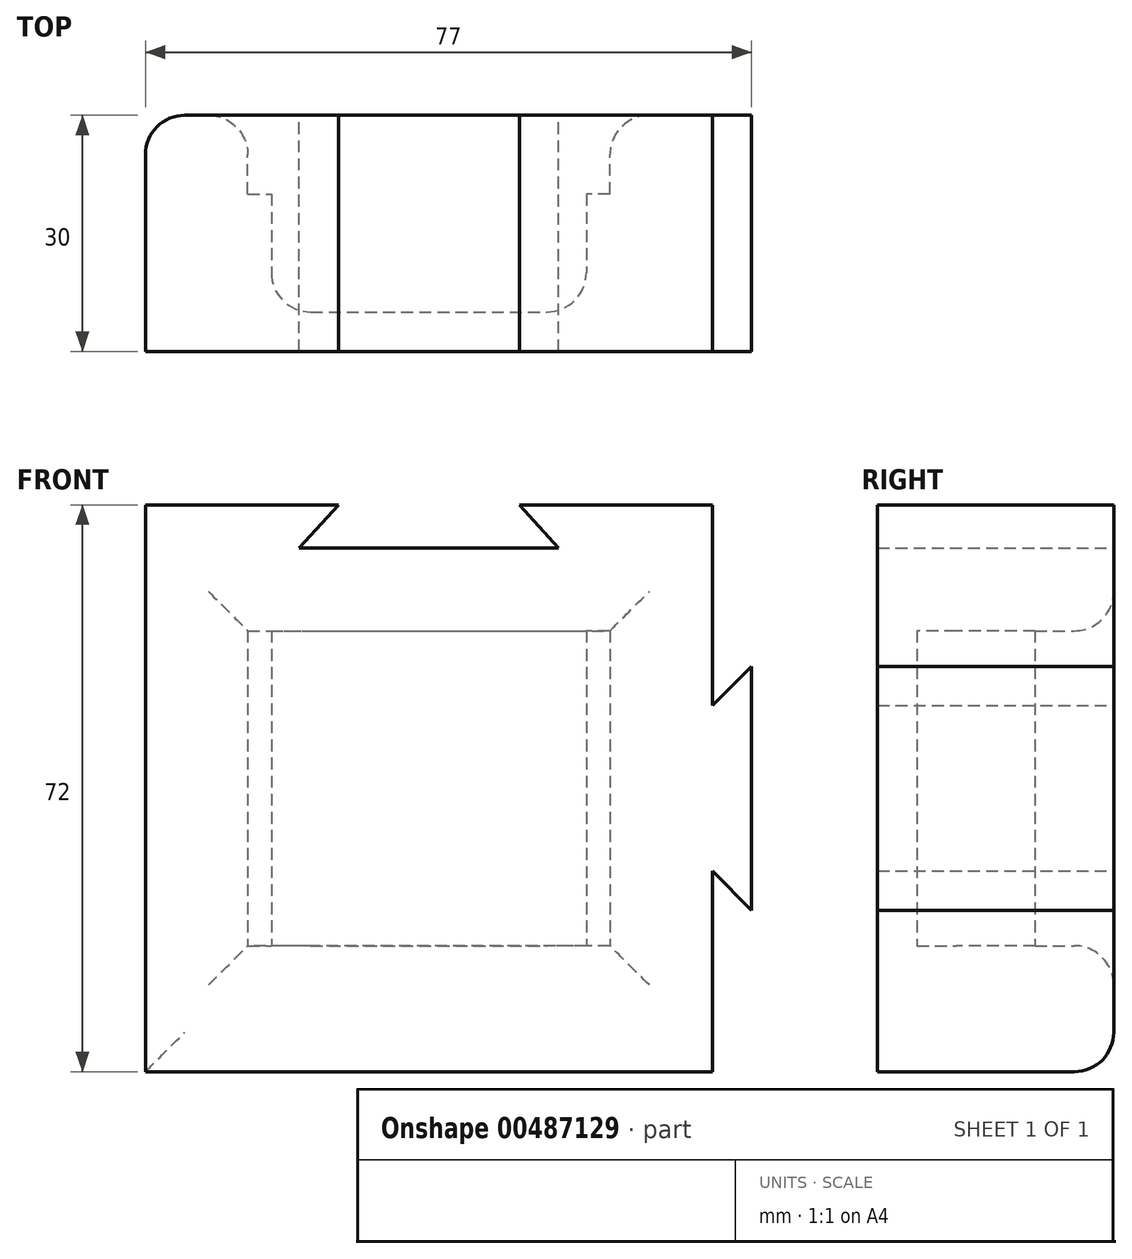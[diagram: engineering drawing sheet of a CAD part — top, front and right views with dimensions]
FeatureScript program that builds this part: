
annotation { "Feature Type Name" : "Feature", "Feature Type Description" : "" }
export const myFeature = defineFeature(function(context is Context, id is Id, definition is map)
    precondition{}
    {
        {
            var Q0;
            Q0=qCreatedBy(makeId("Top.planeOp"),FACE);
            var sketch = newSketch(context, id + "F0", { "sketchPlane" : qUnion([Q0])});
            skLineSegment(sketch, "E0.top", {"start": v(-25, -20) * mm, "end": v(25, -20) * mm});
            skLineSegment(sketch, "E0.left", {"start": v(-25, 0) * mm, "end": v(-25, -20) * mm});
            skLineSegment(sketch, "E0.right", {"start": v(25, 0) * mm, "end": v(25, -20) * mm});
            skLineSegment(sketch, "E1.bottom", {"start": v(-25, 0) * mm, "end": v(-23, 0) * mm});
            skLineSegment(sketch, "E1.top", {"start": v(-25, 10) * mm, "end": v(-23, 10) * mm});
            skLineSegment(sketch, "E1.left", {"start": v(-25, 0) * mm, "end": v(-25, 10) * mm});
            skLineSegment(sketch, "E1.right", {"start": v(-23, 0) * mm, "end": v(-23, 10) * mm});
            skLineSegment(sketch, "E2.bottom", {"start": v(25, 0) * mm, "end": v(23, 0) * mm});
            skLineSegment(sketch, "E2.top", {"start": v(25, 10) * mm, "end": v(23, 10) * mm});
            skLineSegment(sketch, "E2.left", {"start": v(25, 0) * mm, "end": v(25, 10) * mm});
            skLineSegment(sketch, "E2.right", {"start": v(23, 0) * mm, "end": v(23, 10) * mm});
            skLineSegment(sketch, "E3", {"start": v(-25, 0) * mm, "end": v(-20, 0) * mm});
            skLineSegment(sketch, "E4", {"start": v(25, 0) * mm, "end": v(20, 0) * mm});
            skLineSegment(sketch, "E5.bottom", {"start": v(-20, 0) * mm, "end": v(20, 0) * mm});
            skLineSegment(sketch, "E5.top", {"start": v(-20, -15) * mm, "end": v(20, -15) * mm});
            skLineSegment(sketch, "E5.left", {"start": v(-20, 0) * mm, "end": v(-20, -15) * mm});
            skLineSegment(sketch, "E5.right", {"start": v(20, 0) * mm, "end": v(20, -15) * mm});
            skSolve(sketch);
        }
        {
            var Q0;
            Q0=makeQuery(id+"F0.imprint","IMPRINT",FACE,{"disambiguationData":[TD([[makeQuery(id+"F0.imprint","IMPRINT",EDGE,{"derivedFrom":sQuery(id+"F0.wireOp",EDGE,"E1.top")}),-1.0]])]});
            var Q1;
            Q1=makeQuery(id+"F0.imprint","IMPRINT",FACE,{"disambiguationData":[TD([[makeQuery(id+"F0.imprint","IMPRINT",EDGE,{"derivedFrom":sQuery(id+"F0.wireOp",EDGE,"E2.top")}),1.0]])]});
            var Q2;
            Q2=makeQuery(id+"F0.imprint","IMPRINT",FACE,{"disambiguationData":[TD([[makeQuery(id+"F0.imprint","IMPRINT",EDGE,{"derivedFrom":sQuery(id+"F0.wireOp",EDGE,"E0.top")}),1.0]])]});
            extrude(context, id + "F1", {"entities" : qUnion([Q0, Q1, Q2]), "depth" : 40 * mm});
        }
        {
            var Q0;
            Q0=makeQuery(id+"F1.opExtrude","CAP_FACE",FACE,{"disambiguationData":[OSD([sQuery(id+"F0.wireOp",EDGE,"E0.top"),sQuery(id+"F0.wireOp",EDGE,"E0.left"),sQuery(id+"F0.wireOp",EDGE,"E0.right"),sQuery(id+"F0.wireOp",EDGE,"99edbcf1-32be-412c-bc92-f7043755eeb8.trimOffspring"),sQuery(id+"F0.wireOp",EDGE,"E1.top"),sQuery(id+"F0.wireOp",EDGE,"E1.left"),sQuery(id+"F0.wireOp",EDGE,"E1.right"),sQuery(id+"F0.wireOp",EDGE,"E2.top"),sQuery(id+"F0.wireOp",EDGE,"E2.left"),sQuery(id+"F0.wireOp",EDGE,"E2.right"),sQuery(id+"F0.wireOp",EDGE,"E3"),sQuery(id+"F0.wireOp",EDGE,"AQl3pC6e-wCTG-qIrR-r3pU-YnEMlh3t2a7q")])],"isStart":false});
            var sketch = newSketch(context, id + "F2", { "sketchPlane" : qUnion([Q0])});
            skLineSegment(sketch, "E6.bottom", {"start": v(-25, 10) * mm, "end": v(25, 10) * mm});
            skLineSegment(sketch, "E6.top", {"start": v(-25, -20) * mm, "end": v(25, -20) * mm});
            skLineSegment(sketch, "E6.left", {"start": v(-25, 10) * mm, "end": v(-25, -20) * mm});
            skLineSegment(sketch, "E6.right", {"start": v(25, 10) * mm, "end": v(25, -20) * mm});
            skSolve(sketch);
        }
        {
            var Q0;
            Q0 = qSketchRegion(id + "F2", true);
            extrude(context, id + "F3", {"entities" : qUnion([Q0]), "operationType" : NewBodyOperationType.ADD, "depth" : 5 * mm});
        }
        {
            var Q0;
            Q0=makeQuery(id+"F1.opExtrude","CAP_FACE",FACE,{"disambiguationData":[OSD([sQuery(id+"F0.wireOp",EDGE,"E0.top"),sQuery(id+"F0.wireOp",EDGE,"E0.left"),sQuery(id+"F0.wireOp",EDGE,"E0.right"),sQuery(id+"F0.wireOp",EDGE,"99edbcf1-32be-412c-bc92-f7043755eeb8.trimOffspring"),sQuery(id+"F0.wireOp",EDGE,"E1.top"),sQuery(id+"F0.wireOp",EDGE,"E1.left"),sQuery(id+"F0.wireOp",EDGE,"E1.right"),sQuery(id+"F0.wireOp",EDGE,"E2.top"),sQuery(id+"F0.wireOp",EDGE,"E2.left"),sQuery(id+"F0.wireOp",EDGE,"E2.right"),sQuery(id+"F0.wireOp",EDGE,"E3"),sQuery(id+"F0.wireOp",EDGE,"AQl3pC6e-wCTG-qIrR-r3pU-YnEMlh3t2a7q")])],"isStart":true});
            var sketch = newSketch(context, id + "F4", { "sketchPlane" : qUnion([Q0])});
            skLineSegment(sketch, "E7.bottom", {"start": v(25, -10) * mm, "end": v(-25, -10) * mm});
            skLineSegment(sketch, "E7.top", {"start": v(25, 20) * mm, "end": v(-25, 20) * mm});
            skLineSegment(sketch, "E7.left", {"start": v(25, -10) * mm, "end": v(25, 20) * mm});
            skLineSegment(sketch, "E7.right", {"start": v(-25, -10) * mm, "end": v(-25, 20) * mm});
            skSolve(sketch);
        }
        {
            var Q0;
            Q0 = qSketchRegion(id + "F4", true);
            extrude(context, id + "F5", {"entities" : qUnion([Q0]), "operationType" : NewBodyOperationType.ADD, "depth" : 5 * mm});
        }
        {
            var Q0;
            Q0=makeQuery(id+"F5.boolean.opBoolean","MERGE",FACE,{"derivedFrom":[makeQuery(id+"F3.boolean.opBoolean","MERGE",FACE,{"derivedFrom":[makeQuery(id+"F1.opExtrude","SWEPT_FACE",FACE,{"disambiguationData":[OSD([sQuery(id+"F0.wireOp",EDGE,"E1.top")])]}),makeQuery(id+"F1.opExtrude","SWEPT_FACE",FACE,{"disambiguationData":[OSD([sQuery(id+"F0.wireOp",EDGE,"E2.top")])]}),makeQuery(id+"F3.opExtrude","SWEPT_FACE",FACE,{"disambiguationData":[OSD([sQuery(id+"F2.wireOp",EDGE,"E6.bottom")])]})]}),makeQuery(id+"F5.opExtrude","SWEPT_FACE",FACE,{"disambiguationData":[OSD([sQuery(id+"F4.wireOp",EDGE,"E7.bottom")])]})]});
            var sketch = newSketch(context, id + "F6", { "sketchPlane" : qUnion([Q0])});
            skLineSegment(sketch, "E8.bottom", {"start": v(-25, -5) * mm, "end": v(25, -5) * mm});
            skLineSegment(sketch, "E8.top", {"start": v(-25, 45) * mm, "end": v(25, 45) * mm});
            skLineSegment(sketch, "E8.left", {"start": v(-25, -5) * mm, "end": v(-25, 45) * mm});
            skLineSegment(sketch, "E8.right", {"start": v(25, -5) * mm, "end": v(25, 45) * mm});
            skLineSegment(sketch, "E9.bottom", {"start": v(-36, -16) * mm, "end": v(36, -16) * mm});
            skLineSegment(sketch, "E9.top", {"start": v(-36, 56) * mm, "end": v(36, 56) * mm});
            skLineSegment(sketch, "E9.left", {"start": v(-36, -16) * mm, "end": v(-36, 56) * mm});
            skLineSegment(sketch, "E9.right", {"start": v(36, -16) * mm, "end": v(36, 56) * mm});
            skLineSegment(sketch, "E10", {"start": v(-36, 30.5) * mm, "end": v(-41, 35.5) * mm});
            skLineSegment(sketch, "E11", {"start": v(-41, 35.5) * mm, "end": v(-41, 4.5) * mm});
            skLineSegment(sketch, "E12", {"start": v(-41, 4.5) * mm, "end": v(-36, 9.5) * mm});
            skLineSegment(sketch, "E13", {"start": v(-11.5, 56) * mm, "end": v(-16.5, 50.5) * mm});
            skLineSegment(sketch, "E14", {"start": v(-16.5, 50.5) * mm, "end": v(16.5, 50.5) * mm});
            skLineSegment(sketch, "E15", {"start": v(16.5, 50.5) * mm, "end": v(11.5, 56) * mm});
            skSolve(sketch);
        }
        {
            var Q0;
            Q0=makeQuery(id+"F6.imprint","IMPRINT",FACE,{"disambiguationData":[TD([[makeQuery(id+"F6.imprint","IMPRINT",EDGE,{"derivedFrom":sQuery(id+"F6.wireOp",EDGE,"E8.bottom")}),-1.0]])]});
            var Q1;
            {var subQ0=sQuery(id+"F6.wireOp",EDGE,"bd9114eb-aa3e-475a-bfc4-32b6f7a4fe9d");Q1=makeQuery(id+"F6.imprint","IMPRINT",FACE,{"disambiguationData":[TD([[makeQuery(id+"F6.imprint","IMPRINT",EDGE,{"derivedFrom":subQ0}),-1.0]])]});}
            var Q2;
            {var subQ0=sQuery(id+"F6.wireOp",EDGE,"E10");Q2=makeQuery(id+"F6.imprint","IMPRINT",FACE,{"disambiguationData":[TD([[makeQuery(id+"F6.imprint","IMPRINT",EDGE,{"derivedFrom":subQ0}),1.0]])]});}
            extrude(context, id + "F7", {"entities" : qUnion([Q0, Q1, Q2]), "operationType" : NewBodyOperationType.ADD, "oppositeDirection" : true, "depth" : 30 * mm});
        }
        {
            var Q0;
            Q0=makeQuery(id+"F5.opExtrude","CAP_EDGE",EDGE,{"disambiguationData":[OSD([sQuery(id+"F4.wireOp",EDGE,"E7.bottom")])],"isStart":true});
            var Q1;
            Q1=makeQuery(id+"F1.opExtrude","SWEPT_EDGE",EDGE,{"disambiguationData":[OSD([sQuery(id+"F0.wireOp",EDGE,"E2.top"),sQuery(id+"F0.wireOp",EDGE,"E2.right")])]});
            var Q2;
            Q2=makeQuery(id+"F3.opExtrude","CAP_EDGE",EDGE,{"disambiguationData":[OSD([sQuery(id+"F2.wireOp",EDGE,"E6.bottom")])],"isStart":true});
            var Q3;
            Q3=makeQuery(id+"F1.opExtrude","SWEPT_EDGE",EDGE,{"disambiguationData":[OSD([sQuery(id+"F0.wireOp",EDGE,"E1.top"),sQuery(id+"F0.wireOp",EDGE,"E1.right")])]});
            var Q4;
            Q4=makeQuery(id+"F7.opExtrude","CAP_EDGE",EDGE,{"disambiguationData":[OSD([sQuery(id+"F6.wireOp",EDGE,"E9.right")])],"isStart":true});
            var Q5;
            Q5=makeQuery(id+"F7.opExtrude","CAP_EDGE",EDGE,{"disambiguationData":[OSD([sQuery(id+"F6.wireOp",EDGE,"E9.bottom")])],"isStart":true});
            fillet(context, id + "F8", {"entities" : qUnion([Q0, Q1, Q2, Q3, Q4, Q5]), "radius" : 5 * mm, "tangentPropagation" : true, "allowEdgeOverflow" : false});
        }
        {
            var Q0;
            Q0=makeQuery(id+"F1.opExtrude","SWEPT_EDGE",EDGE,{"disambiguationData":[OSD([sQuery(id+"F0.wireOp",EDGE,"E5.top"),sQuery(id+"F0.wireOp",EDGE,"E5.right")])]});
            var Q1;
            Q1=makeQuery(id+"F1.opExtrude","CAP_EDGE",EDGE,{"disambiguationData":[OSD([sQuery(id+"F0.wireOp",EDGE,"E5.top")])],"isStart":true});
            var Q2;
            Q2=makeQuery(id+"F1.opExtrude","CAP_EDGE",EDGE,{"disambiguationData":[OSD([sQuery(id+"F0.wireOp",EDGE,"E5.top")])],"isStart":false});
            var Q3;
            Q3=makeQuery(id+"F1.opExtrude","SWEPT_EDGE",EDGE,{"disambiguationData":[OSD([sQuery(id+"F0.wireOp",EDGE,"E5.top"),sQuery(id+"F0.wireOp",EDGE,"E5.left")])]});
            fillet(context, id + "F9", {"entities" : qUnion([Q0, Q1, Q2, Q3]), "radius" : 5 * mm, "tangentPropagation" : true, "allowEdgeOverflow" : false});
        }
    });
